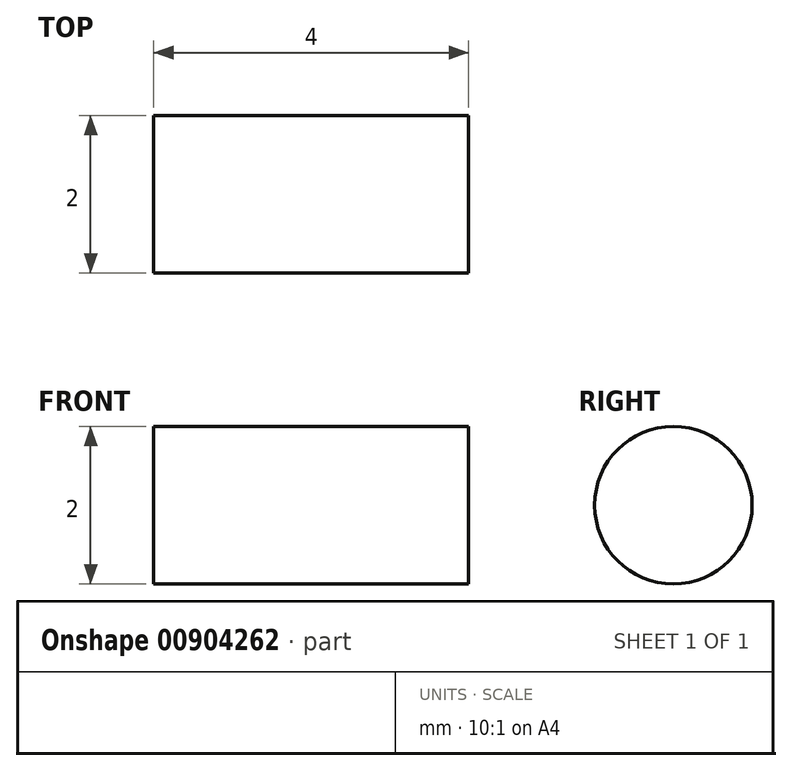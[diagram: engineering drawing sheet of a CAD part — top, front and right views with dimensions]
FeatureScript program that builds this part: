
annotation { "Feature Type Name" : "Feature", "Feature Type Description" : "" }
export const myFeature = defineFeature(function(context is Context, id is Id, definition is map)
    precondition{}
    {
        {
            var Q0;
            Q0=qCreatedBy(makeId("Front.planeOp"),FACE);
            var sketch = newSketch(context, id + "F0", { "sketchPlane" : qUnion([Q0])});
            skLineSegment(sketch, "E0.bottom", {"start": v(0, 0) * mm, "end": v(-3, 0) * mm});
            skLineSegment(sketch, "E0.top", {"start": v(0, 1) * mm, "end": v(-3, 1) * mm});
            skLineSegment(sketch, "E0.left", {"start": v(0, 0) * mm, "end": v(0, 1) * mm});
            skLineSegment(sketch, "E0.right", {"start": v(-3, 0) * mm, "end": v(-3, 1) * mm});
            skLineSegment(sketch, "E1.bottom", {"start": v(-3, 0) * mm, "end": v(-3.5, 0) * mm});
            skLineSegment(sketch, "E1.top", {"start": v(-3, 1) * mm, "end": v(-3.5, 1) * mm});
            skLineSegment(sketch, "E1.right", {"start": v(-3.5, 0) * mm, "end": v(-3.5, 1) * mm});
            skLineSegment(sketch, "E2.bottom", {"start": v(0, 0) * mm, "end": v(0.5, 0) * mm});
            skLineSegment(sketch, "E2.top", {"start": v(0, 1) * mm, "end": v(0.5, 1) * mm});
            skLineSegment(sketch, "E2.right", {"start": v(0.5, 0) * mm, "end": v(0.5, 1) * mm});
            skSolve(sketch);
        }
        {
            var Q0;
            Q0=makeQuery(id+"F0.imprint","IMPRINT",FACE,{"disambiguationData":[TD([[makeQuery(id+"F0.imprint","IMPRINT",EDGE,{"derivedFrom":sQuery(id+"F0.wireOp",EDGE,"E0.bottom")}),-1.0]])]});
            var Q1;
            Q1=makeQuery(id+"F0.imprint","IMPRINT",FACE,{"disambiguationData":[TD([[makeQuery(id+"F0.imprint","IMPRINT",EDGE,{"derivedFrom":sQuery(id+"F0.wireOp",EDGE,"E1.bottom")}),-1.0]])]});
            var Q2;
            Q2=makeQuery(id+"F0.imprint","IMPRINT",FACE,{"disambiguationData":[TD([[makeQuery(id+"F0.imprint","IMPRINT",EDGE,{"derivedFrom":sQuery(id+"F0.wireOp",EDGE,"E2.bottom")}),1.0]])]});
            var Q3;
            Q3=sQuery(id+"F0.wireOp",EDGE,"E0.bottom");
            revolve(context, id + "F1", {"surfaceOperationType" : NewSurfaceOperationType.NEW, "entities" : qUnion([Q0, Q1, Q2]), "axis" : qUnion([Q3]), "revolveType" : RevolveType.FULL});
        }
    });
